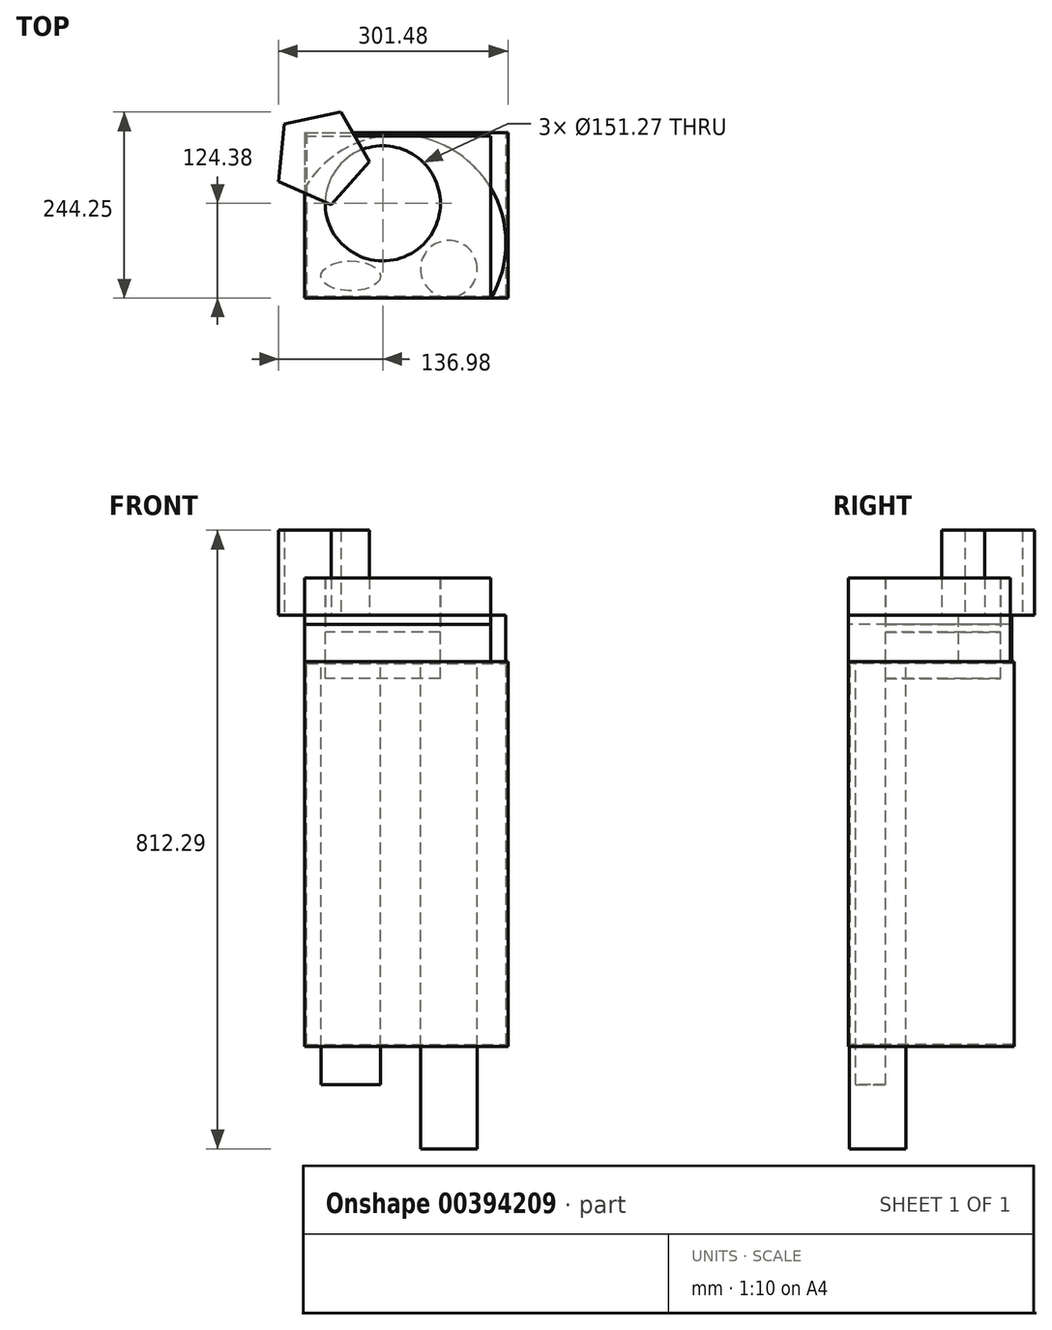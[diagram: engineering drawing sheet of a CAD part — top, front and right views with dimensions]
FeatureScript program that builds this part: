
annotation { "Feature Type Name" : "Feature", "Feature Type Description" : "" }
export const myFeature = defineFeature(function(context is Context, id is Id, definition is map)
    precondition{}
    {
        {
            var Q0;
            Q0=qCreatedBy(makeId("Top.planeOp"),FACE);
            var sketch = newSketch(context, id + "F0", { "sketchPlane" : qUnion([Q0])});
            skCircle(sketch, "E0", {"center": v(0, 0) * mm, "radius": 75.63 * mm});
            skSolve(sketch);
        }
        {
            var Q0;
            Q0 = qSketchRegion(id + "F0", true);
            extrude(context, id + "F1", {"entities" : qUnion([Q0]), "depth" : 22.1 * mm});
        }
        {
            var Q0;
            Q0=makeQuery(id+"F1.opExtrude","CAP_FACE",FACE,{"disambiguationData":[OSD([sQuery(id+"F0.wireOp",EDGE,"E0")])],"isStart":false});
            var sketch = newSketch(context, id + "F2", { "sketchPlane" : qUnion([Q0])});
            skLineSegment(sketch, "E1.bottom", {"start": v(-122.72, 65.43) * mm, "end": v(-120.96, 65.43) * mm});
            skLineSegment(sketch, "E1.top", {"start": v(-122.72, 77.02) * mm, "end": v(-120.96, 77.02) * mm});
            skLineSegment(sketch, "E2.bottom", {"start": v(-102.5, 88.39) * mm, "end": v(141.96, 88.39) * mm});
            skLineSegment(sketch, "E2.top", {"start": v(-102.5, -124.38) * mm, "end": v(141.96, -124.38) * mm});
            skLineSegment(sketch, "E2.left", {"start": v(-102.5, 88.39) * mm, "end": v(-102.5, -124.38) * mm});
            skLineSegment(sketch, "E2.right", {"start": v(141.96, 88.39) * mm, "end": v(141.96, -124.38) * mm});
            skSolve(sketch);
        }
        {
            var Q0;
            Q0=makeQuery(id+"F2.imprint","IMPRINT",FACE,{"disambiguationData":[TD([[makeQuery(id+"F2.imprint","IMPRINT",EDGE,{"derivedFrom":sQuery(id+"F2.wireOp",EDGE,"E2.bottom")}),-1.0]])]});
            extrude(context, id + "F3", {"entities" : qUnion([Q0]), "depth" : 49.28 * mm});
        }
        {
            var Q0;
            Q0=makeQuery(id+"F3.opExtrude","CAP_FACE",FACE,{"disambiguationData":[OSD([sQuery(id+"F0.wireOp",EDGE,"E0"),sQuery(id+"F2.wireOp",EDGE,"E2.bottom"),sQuery(id+"F2.wireOp",EDGE,"E2.top"),sQuery(id+"F2.wireOp",EDGE,"E2.left"),sQuery(id+"F2.wireOp",EDGE,"E2.right")])],"isStart":true});
            var sketch = newSketch(context, id + "F4", { "sketchPlane" : qUnion([Q0])});
            skArc(sketch, "E3", {"start": v(-102.5, 124.38) * mm, "mid": v(19.73, -89.98) * mm, "end": v(141.96, 124.38) * mm});
            skSolve(sketch);
        }
        {
            var Q0;
            Q0 = qSketchRegion(id + "F4", true);
            var Q1;
            {var subQ0=sQuery(id+"F4.wireOp",EDGE,"E3");var subQ1=makeQuery(id+"F3.opExtrude","CAP_EDGE",EDGE,{"disambiguationData":[OSD([sQuery(id+"F2.wireOp",EDGE,"E2.bottom")])],"isStart":true});var subQ2=makeQuery(id+"F4.imprint","INTERSECT",VERTEX,{"disambiguationData":[OD(0.0)],"derivedFrom":[subQ1,subQ0]});Q1=makeQuery(id+"F4.imprint","IMPRINT",FACE,{"disambiguationData":[TD([[makeQuery(id+"F4.imprint","IMPRINT",EDGE,{"disambiguationData":[TD([[subQ2,-1.0]])],"derivedFrom":subQ0}),1.0]])]});}
            var Q2;
            {var subQ0=sQuery(id+"F4.wireOp",EDGE,"E3");var subQ1=makeQuery(id+"F3.opExtrude","CAP_EDGE",EDGE,{"disambiguationData":[OSD([sQuery(id+"F2.wireOp",EDGE,"E2.right")])],"isStart":true});var subQ3=makeQuery(id+"F4.imprint","INTERSECT",VERTEX,{"derivedFrom":[subQ1,subQ0]});Q2=makeQuery(id+"F4.imprint","IMPRINT",FACE,{"disambiguationData":[TD([[makeQuery(id+"F4.imprint","IMPRINT",EDGE,{"disambiguationData":[TD([[subQ3,-1.0]])],"derivedFrom":subQ0}),1.0]])]});}
            var Q3;
            {var subQ0=makeQuery(id+"F3.opExtrude","CAP_EDGE",EDGE,{"disambiguationData":[OSD([sQuery(id+"F2.wireOp",EDGE,"E2.top")])],"isStart":true});Q3=makeQuery(id+"F4.imprint","IMPRINT",FACE,{"disambiguationData":[TD([[makeQuery(id+"F4.imprint","IMPRINT",EDGE,{"derivedFrom":subQ0}),-1.0]])]});}
            var Q4;
            Q4=makeQuery(id+"F3.opExtrude","CAP_FACE",FACE,{"disambiguationData":[OSD([sQuery(id+"F0.wireOp",EDGE,"E0"),sQuery(id+"F2.wireOp",EDGE,"E2.bottom"),sQuery(id+"F2.wireOp",EDGE,"E2.top"),sQuery(id+"F2.wireOp",EDGE,"E2.left"),sQuery(id+"F2.wireOp",EDGE,"E2.right")])],"isStart":true});
            var Q5;
            Q5=makeQuery(id+"F1.opExtrude","CAP_FACE",FACE,{"disambiguationData":[OSD([sQuery(id+"F0.wireOp",EDGE,"E0")])],"isStart":true});
            var Q6;
            Q6=makeQuery(id+"F4.imprint","IMPRINT",FACE,{"disambiguationData":[TD([[makeQuery(id+"F4.imprint","IMPRINT",EDGE,{"derivedFrom":makeQuery(id+"F3.opExtrude","CAP_EDGE",EDGE,{"disambiguationData":[OSD([sQuery(id+"F0.wireOp",EDGE,"E0")])],"isStart":true})}),-1.0]])]});
            var Q7;
            Q7=makeQuery(id+"F3.opExtrude","CAP_FACE",FACE,{"disambiguationData":[OSD([sQuery(id+"F0.wireOp",EDGE,"E0"),sQuery(id+"F2.wireOp",EDGE,"E2.bottom"),sQuery(id+"F2.wireOp",EDGE,"E2.top"),sQuery(id+"F2.wireOp",EDGE,"E2.left"),sQuery(id+"F2.wireOp",EDGE,"E2.right")])],"isStart":false});
            var Q8;
            Q8=makeQuery(id+"F1.opExtrude","CAP_FACE",FACE,{"disambiguationData":[OSD([sQuery(id+"F0.wireOp",EDGE,"E0")])],"isStart":false});
            extrude(context, id + "F5", {"entities" : qUnion([Q0, Q1, Q2, Q3, Q4, Q5, Q6, Q7, Q8]), "depth" : 60.96 * mm});
        }
        {
            var Q0;
            Q0=makeQuery(id+"F5.opExtrude","CAP_FACE",FACE,{"disambiguationData":[OSD([sQuery(id+"F2.wireOp",EDGE,"E2.top"),sQuery(id+"F2.wireOp",EDGE,"E2.left"),sQuery(id+"F4.wireOp",EDGE,"E3")])],"isStart":true});
            var sketch = newSketch(context, id + "F6", { "sketchPlane" : qUnion([Q0])});
            skLineSegment(sketch, "E4", {"start": v(-88.29, 20.79) * mm, "end": v(51.38, 12.83) * mm});
            skSolve(sketch);
        }
        {
            var Q0;
            {var subQ0=sQuery(id+"F2.wireOp",EDGE,"E2.right");var subQ1=sQuery(id+"F2.wireOp",EDGE,"E2.left");var subQ2=sQuery(id+"F2.wireOp",EDGE,"E2.top");var subQ3=sQuery(id+"F2.wireOp",EDGE,"E2.bottom");var subQ4=sQuery(id+"F0.wireOp",EDGE,"E0");Q0=makeQuery(id+"F5.opExtrude","CAP_FACE",FACE,{"disambiguationData":[OSD([subQ4,subQ3,subQ2,subQ1,subQ0]),TDD([makeQuery(id+"F3.opExtrude","CAP_FACE",FACE,{"disambiguationData":[OSD([subQ4,subQ3,subQ2,subQ1,subQ0])],"isStart":true})])],"isStart":false});}
            var sketch = newSketch(context, id + "F7", { "sketchPlane" : qUnion([Q0])});
            skCircle(sketch, "E5", {"center": v(86.72, 86.03) * mm, "radius": 37.28 * mm});
            skPoint(sketch, "E5.first.point", {"position": v(54.5, 104.79) * mm});
            skPoint(sketch, "E5.second.point", {"position": v(119.7, 68.64) * mm});
            skPoint(sketch, "E5.third.point", {"position": v(123.85, 82.68) * mm});
            skSolve(sketch);
        }
        {
            var Q0;
            Q0=makeQuery(id+"F7.imprint","IMPRINT",FACE,{"disambiguationData":[TD([[makeQuery(id+"F7.imprint","IMPRINT",EDGE,{"derivedFrom":sQuery(id+"F7.wireOp",EDGE,"E5")}),1.0]])]});
            extrude(context, id + "F8", {"entities" : qUnion([Q0]), "depth" : 639.57 * mm});
        }
        {
            var Q0;
            {var subQ0=sQuery(id+"F2.wireOp",EDGE,"E2.right");var subQ1=sQuery(id+"F2.wireOp",EDGE,"E2.left");var subQ2=sQuery(id+"F2.wireOp",EDGE,"E2.top");var subQ3=sQuery(id+"F2.wireOp",EDGE,"E2.bottom");var subQ4=sQuery(id+"F0.wireOp",EDGE,"E0");Q0=makeQuery(id+"F5.opExtrude","CAP_FACE",FACE,{"disambiguationData":[OSD([subQ4,subQ3,subQ2,subQ1,subQ0]),TDD([makeQuery(id+"F3.opExtrude","CAP_FACE",FACE,{"disambiguationData":[OSD([subQ4,subQ3,subQ2,subQ1,subQ0])],"isStart":true})])],"isStart":false});}
            var sketch = newSketch(context, id + "F9", { "sketchPlane" : qUnion([Q0])});
            skEllipse(sketch, "E6", {"center": v(-42.16, 95.29) * mm, "majorRadius": 39.1 * mm, "minorRadius": 19.64 * mm, "majorAxis": v(1, 0)});
            skSolve(sketch);
        }
        {
            var Q0;
            Q0 = qSketchRegion(id + "F9", true);
            extrude(context, id + "F10", {"entities" : qUnion([Q0]), "depth" : 555.5 * mm});
        }
        {
            var Q0;
            Q0=makeQuery(id+"F5.opExtrude","CAP_FACE",FACE,{"disambiguationData":[OSD([sQuery(id+"F2.wireOp",EDGE,"E2.top"),sQuery(id+"F2.wireOp",EDGE,"E2.left"),sQuery(id+"F4.wireOp",EDGE,"E3")])],"isStart":false});
            var sketch = newSketch(context, id + "F11", { "sketchPlane" : qUnion([Q0])});
            skLineSegment(sketch, "E7.bottom", {"start": v(-102.5, 124.38) * mm, "end": v(164.5, 124.38) * mm});
            skLineSegment(sketch, "E7.top", {"start": v(-102.5, -93.11) * mm, "end": v(164.5, -93.11) * mm});
            skLineSegment(sketch, "E7.left", {"start": v(-102.5, 124.38) * mm, "end": v(-102.5, -93.11) * mm});
            skLineSegment(sketch, "E7.right", {"start": v(164.5, 124.38) * mm, "end": v(164.5, -93.11) * mm});
            skSolve(sketch);
        }
        {
            var Q0;
            Q0 = qSketchRegion(id + "F11", true);
            extrude(context, id + "F12", {"entities" : qUnion([Q0]), "depth" : 505.46 * mm});
        }
        {
            var Q0;
            Q0=makeQuery(id+"F12.opExtrude","SWEPT_FACE",FACE,{"disambiguationData":[OSD([sQuery(id+"F11.wireOp",EDGE,"E7.top")])]});
            shell(context, id + "F13", {"entities" : qUnion([Q0]), "thickness" : 2.54 * mm});
        }
        {
            var Q0;
            {var subQ0=sQuery(id+"F4.wireOp",EDGE,"E3");Q0=makeQuery(id+"F6.imprint","IMPRINT",FACE,{"disambiguationData":[TD([[makeQuery(id+"F6.imprint","IMPRINT",EDGE,{"derivedFrom":makeQuery(id+"F5.opExtrude","CAP_EDGE",EDGE,{"disambiguationData":[OSD([subQ0])],"isStart":true})}),-1.0]])]});}
            var sketch = newSketch(context, id + "F14", { "sketchPlane" : qUnion([Q0])});
            skCircle(sketch, "E8.cCircle", {"center": v(-81.39, 61.08) * mm, "radius": 64.28 * mm, "construction": true});
            skLineSegment(sketch, "E8.0", {"start": v(-129.26, 103.98) * mm, "end": v(-55.39, 119.87) * mm});
            skLineSegment(sketch, "E8.1", {"start": v(-55.39, 119.87) * mm, "end": v(-17.45, 54.52) * mm});
            skLineSegment(sketch, "E8.2", {"start": v(-17.45, 54.52) * mm, "end": v(-67.87, -1.76) * mm});
            skLineSegment(sketch, "E8.3", {"start": v(-67.87, -1.76) * mm, "end": v(-136.98, 28.8) * mm});
            skLineSegment(sketch, "E8.4", {"start": v(-136.98, 28.8) * mm, "end": v(-129.26, 103.98) * mm});
            skSolve(sketch);
        }
        {
            var Q0;
            Q0 = qSketchRegion(id + "F14", true);
            extrude(context, id + "F15", {"entities" : qUnion([Q0]), "depth" : 111.76 * mm});
        }
    });
